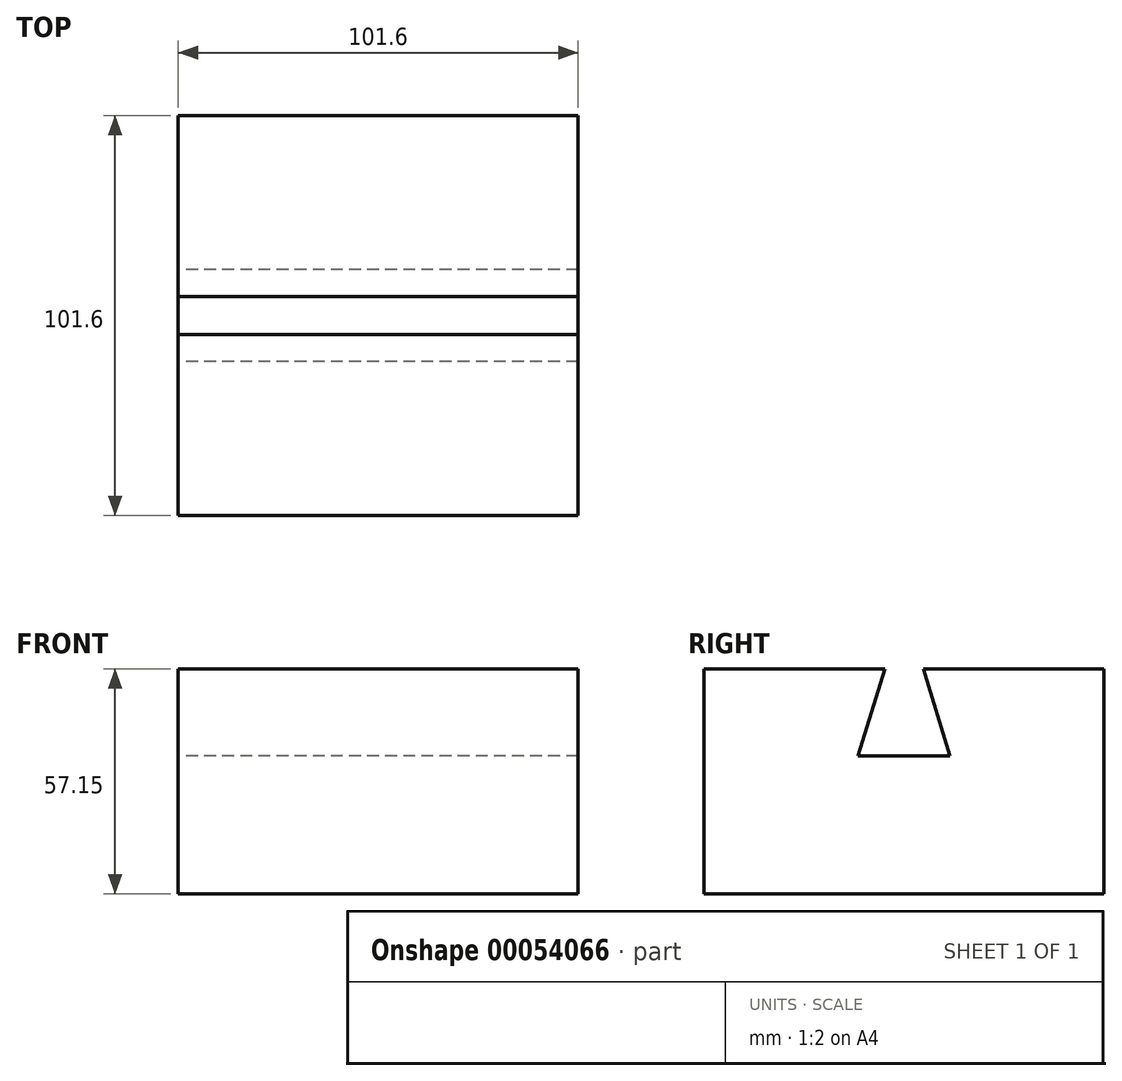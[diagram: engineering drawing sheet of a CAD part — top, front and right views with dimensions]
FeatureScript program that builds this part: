
annotation { "Feature Type Name" : "Feature", "Feature Type Description" : "" }
export const myFeature = defineFeature(function(context is Context, id is Id, definition is map)
    precondition{}
    {
        {
            var Q0;
            Q0=qCreatedBy(makeId("Top.planeOp"),FACE);
            var sketch = newSketch(context, id + "F0", { "sketchPlane" : qUnion([Q0])});
            skLineSegment(sketch, "E0.rect.bottom", {"start": v(50.8, 50.8) * mm, "end": v(-50.8, 50.8) * mm});
            skLineSegment(sketch, "E0.rect.top", {"start": v(50.8, -50.8) * mm, "end": v(-50.8, -50.8) * mm});
            skLineSegment(sketch, "E0.rect.left", {"start": v(50.8, 50.8) * mm, "end": v(50.8, -50.8) * mm});
            skLineSegment(sketch, "E0.rect.right", {"start": v(-50.8, 50.8) * mm, "end": v(-50.8, -50.8) * mm});
            skPoint(sketch, "E0.rect.middle", {"position": v(0, 0) * mm});
            skSolve(sketch);
        }
        {
            var Q0;
            Q0 = qSketchRegion(id + "F0", true);
            extrude(context, id + "F1", {"entities" : qUnion([Q0]), "depth" : 25.4 * mm, "hasSecondDirection" : true, "secondDirectionOppositeDirection" : true, "secondDirectionDepth" : 31.75 * mm});
        }
        {
            var Q0;
            Q0=qCreatedBy(makeId("Right.planeOp"),FACE);
            var sketch = newSketch(context, id + "F2", { "sketchPlane" : qUnion([Q0])});
            skLineSegment(sketch, "E1", {"start": v(-11.7, 3.3) * mm, "end": v(-4.89, 25.4) * mm});
            skPoint(sketch, "E2.orphan", {"position": v(-9.78, 25.4) * mm});
            skLineSegment(sketch, "E3.MirrorCS", {"start": v(11.7, 3.3) * mm, "end": v(4.89, 25.4) * mm});
            skPoint(sketch, "E4.MirrorP", {"position": v(9.78, 25.4) * mm});
            skLineSegment(sketch, "E5", {"start": v(-4.89, 25.4) * mm, "end": v(4.89, 25.4) * mm});
            skLineSegment(sketch, "E6", {"start": v(-11.7, 3.3) * mm, "end": v(11.7, 3.3) * mm});
            skSolve(sketch);
        }
        {
            var Q0;
            Q0 = qSketchRegion(id + "F2", true);
            extrude(context, id + "F3", {"entities" : qUnion([Q0]), "operationType" : NewBodyOperationType.REMOVE, "endBound" : BoundingType.THROUGH_ALL, "depth" : 25.4 * mm, "hasSecondDirection" : true, "secondDirectionBound" : SecondDirectionBoundingType.THROUGH_ALL, "secondDirectionOppositeDirection" : true, "secondDirectionDepth" : 25.4 * mm});
        }
    });
